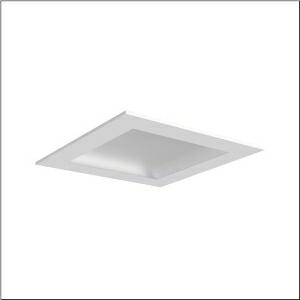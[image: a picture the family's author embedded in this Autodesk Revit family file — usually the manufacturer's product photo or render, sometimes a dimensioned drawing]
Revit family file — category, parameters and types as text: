
# Revit family: mira_r__11_sl_51fr427a453a_4161
name_source: partatom
category: Lighting Fixtures
units: mm (PartAtom-declared; Revit-internal decimal feet)

## family parameters
Cut with Voids When Loaded = No
Host = Face
Light Source = No
Part Type = Normal
Room Calculation Point = No
Round Connector Dimension = Use Diameter
Shared = No

## types (1)
- Mira® 11 SL (1 x LED, 5850 lm, 58 W, 4000K)
    Apparent Load = 58 VA
    CIE Flux Codes = 50 81 97 100 100
    Color Rendering = 80
    Color Temperature = 4000K
    Default Elevation = 1800 mm
    Description = Mira® 11 SL, clean room luminaire, primary light control with reflector, primary optical cover: cover, of PC, light emission: direct distribution, primary light characteristic: symmetric, installation type: recessed, LED, rated luminous flux: 5.850lm, luminous efficacy: 101lm/W, light colour: 840, colour temperature: 4000K, control gear: ON/OFF, with terminal, 3-pole, max. 2.5mm², mains connection: 230V, AC, 50/60Hz, rated input power: 58W, luminaire housing, of sheet steel, coated, pure white (RAL 9010), with wing nuts, module: M625, length: 623mm, width: 623mm, height: 91mm, protection rating (complete): IP54, protection rating (on room side): IP65, insulation class (complete): insulation class I (protective earthing), certification: CE, UKCA, permissible operating ambient temperature: -5..+40°C, standard: EN 50419, packaging unit: 1 piece
    Height = 0 mm  [stored 0 ft]
    Lamp = 1 x LED
    Lamp Light Flux = 5850 lm
    Lamp Power = 58 W
    Lamp count = 1
    Length = 625 mm
    Luminous efficacy = 101 lm/W
    Manufacturer = Siteco
    ModVariant = No
    Model = 51FR427A453A
    Mounting Place = Ceiling
    Mounting Type = Recessed
    Number of Poles = 1
    OnlyDefault = Yes
    Power Factor = 1
    Product Name = Mira® 11 SL
    Product group = clean room luminaire | ceiling recessed
    ProductGroupID = 402
    Protection Class = Protection class I
    Protection Degree = IP 54
    RLX_Detail_Level = 1
    RLX_Emergency_Light_Flux = 0 lm
    RLX_Emergency_Type = 0
    RLX_Emergency_Type_DB = No
    RlxData = <blob elided: 19913 chars, md5=fb44b193>
    Socket = socket
    Standby Power = 0 W
    System Light Flux = 5850 lm
    System Power = 58 W
    Type Comments = Product without accessories
    Type Image = l_1007111.jpg
    URL = http://relux.com
    VarID = ---
    Voltage = 0 V
    Weight = 0.00 kg
    Width = 625 mm

note: [stored X ft] marks values corroborated as IEEE doubles in the binary element streams (Revit-internal decimal feet)

## geometry (parser evidence)
native form markers: Blend x4, Sweep x10
no freeform markers — native parametric forms only
